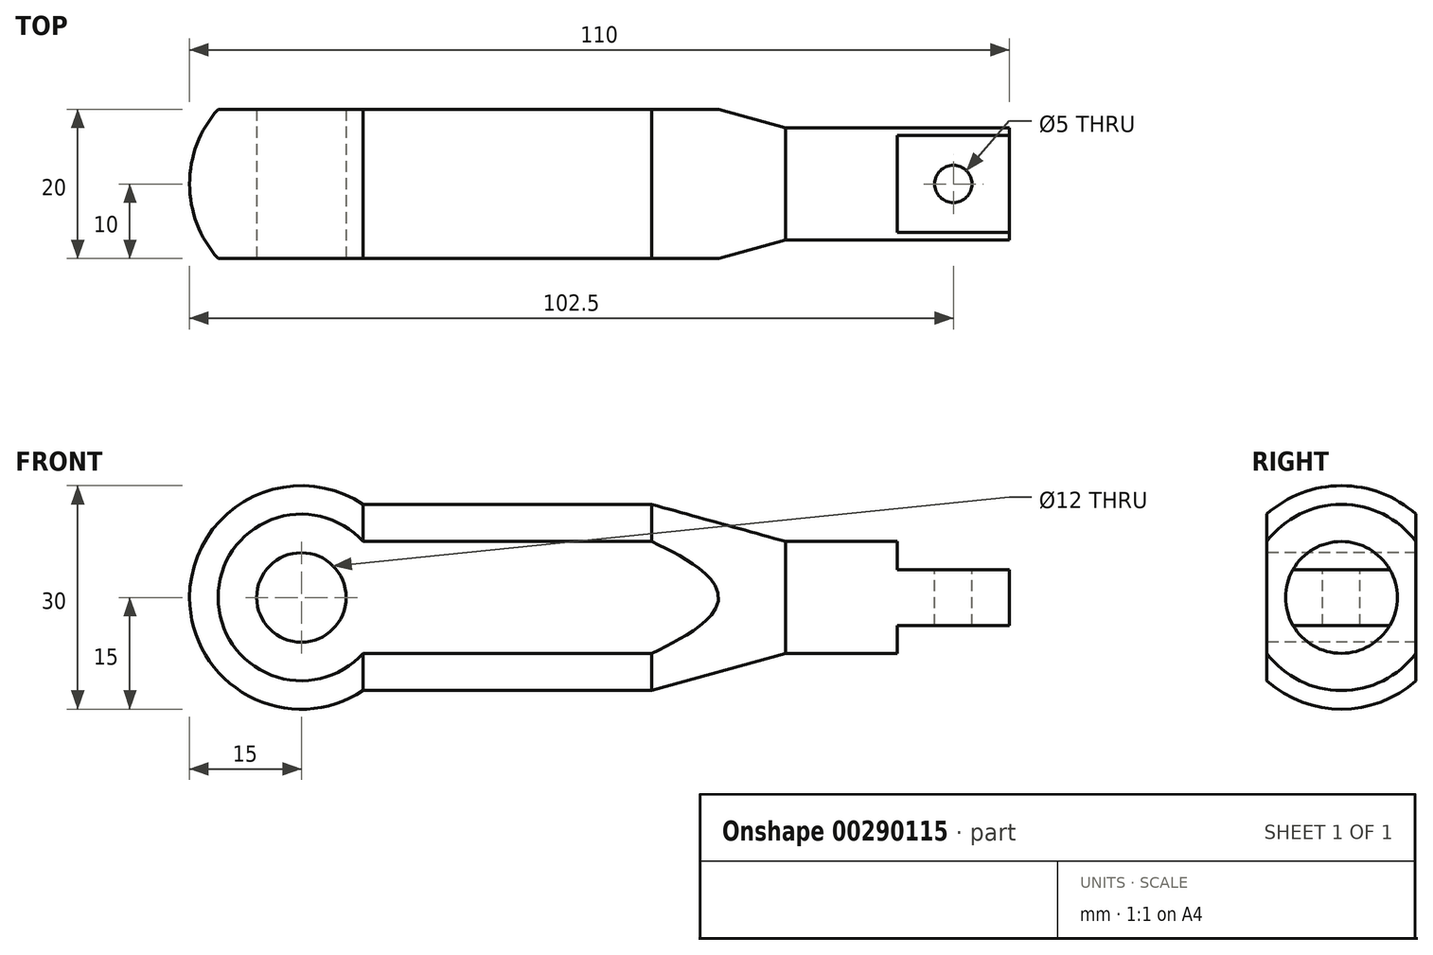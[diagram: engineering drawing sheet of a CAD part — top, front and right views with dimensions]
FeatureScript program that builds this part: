
annotation { "Feature Type Name" : "Feature", "Feature Type Description" : "" }
export const myFeature = defineFeature(function(context is Context, id is Id, definition is map)
    precondition{}
    {
        {
            var Q0;
            Q0=qCreatedBy(makeId("Front.planeOp"),FACE);
            var sketch = newSketch(context, id + "F0", { "sketchPlane" : qUnion([Q0])});
            skLineSegment(sketch, "E0", {"start": v(-47.5, 0) * mm, "end": v(47.5, 0) * mm, "construction": true});
            skLineSegment(sketch, "E1", {"start": v(47.5, 7.5) * mm, "end": v(32.5, 7.5) * mm});
            skLineSegment(sketch, "E2", {"start": v(32.5, 7.5) * mm, "end": v(32.5, 7.5) * mm});
            skLineSegment(sketch, "E3", {"start": v(32.5, 7.5) * mm, "end": v(17.5, 7.5) * mm});
            skLineSegment(sketch, "E4", {"start": v(17.5, 7.5) * mm, "end": v(-0.5, 12.5) * mm});
            skLineSegment(sketch, "E5", {"start": v(-0.5, 12.5) * mm, "end": v(-39.2, 12.5) * mm});
            skCircle(sketch, "E6", {"center": v(-47.5, 0) * mm, "radius": 6 * mm});
            skArc(sketch, "E7", {"start": v(-39.2, 12.5) * mm, "mid": v(-54.6, 13.22) * mm, "end": v(-62.5, 0) * mm});
            skLineSegment(sketch, "E8", {"start": v(-62.5, 0) * mm, "end": v(47.5, 0) * mm});
            skLineSegment(sketch, "E9", {"start": v(32.5, 7.5) * mm, "end": v(32.5, 0) * mm});
            skLineSegment(sketch, "E10", {"start": v(32.5, 0) * mm, "end": v(32.5, -7.5) * mm});
            skLineSegment(sketch, "E11", {"start": v(32.5, -7.5) * mm, "end": v(47.5, -7.5) * mm});
            skLineSegment(sketch, "E12", {"start": v(47.5, 7.5) * mm, "end": v(47.5, -7.5) * mm});
            skLineSegment(sketch, "E13", {"start": v(32.5, 3.75) * mm, "end": v(47.5, 3.75) * mm});
            skLineSegment(sketch, "E14", {"start": v(32.5, -3.75) * mm, "end": v(47.5, -3.75) * mm});
            skSolve(sketch);
        }
        {
            var Q0;
            Q0=qCreatedBy(makeId("Right.planeOp"),FACE);
            var sketch = newSketch(context, id + "F1", { "sketchPlane" : qUnion([Q0])});
            skLineSegment(sketch, "E15", {"start": v(-10, 0) * mm, "end": v(10, 0) * mm});
            skLineSegment(sketch, "E16", {"start": v(-10, 20) * mm, "end": v(-10, -20) * mm});
            skLineSegment(sketch, "E17", {"start": v(10, 20) * mm, "end": v(10, -20) * mm});
            skLineSegment(sketch, "E18", {"start": v(10, 20) * mm, "end": v(60, 20) * mm});
            skLineSegment(sketch, "E19", {"start": v(60, 20) * mm, "end": v(60, -20) * mm});
            skLineSegment(sketch, "E20", {"start": v(60, -20) * mm, "end": v(10, -20) * mm});
            skLineSegment(sketch, "E21", {"start": v(-10, 20) * mm, "end": v(-60, 20) * mm});
            skLineSegment(sketch, "E22", {"start": v(-60, 20) * mm, "end": v(-60, -20) * mm});
            skLineSegment(sketch, "E23", {"start": v(-60, -20) * mm, "end": v(-10, -20) * mm});
            skSolve(sketch);
        }
        {
            var Q0;
            Q0=makeQuery(id+"F0.imprint","IMPRINT",FACE,{"disambiguationData":[TD([[makeQuery(id+"F0.imprint","IMPRINT",EDGE,{"derivedFrom":sQuery(id+"F0.wireOp",EDGE,"E3")}),1.0]])]});
            var Q1;
            {var subQ0=sQuery(id+"F0.wireOp",EDGE,"E1");Q1=makeQuery(id+"F0.imprint","IMPRINT",FACE,{"disambiguationData":[TD([[makeQuery(id+"F0.imprint","IMPRINT",EDGE,{"derivedFrom":subQ0}),1.0]])]});}
            var Q2;
            {var subQ5=sQuery(id+"F0.wireOp",EDGE,"E13");Q2=makeQuery(id+"F0.imprint","IMPRINT",FACE,{"disambiguationData":[TD([[makeQuery(id+"F0.imprint","IMPRINT",EDGE,{"derivedFrom":subQ5}),-1.0]])]});}
            var Q3;
            Q3=sQuery(id+"F0.wireOp",EDGE,"E8");
            revolve(context, id + "F2", {"entities" : qUnion([Q0, Q1, Q2]), "axis" : qUnion([Q3]), "revolveType" : RevolveType.FULL});
        }
        {
            var Q0;
            {var subQ0=sQuery(id+"F0.wireOp",EDGE,"E8");var subQ1=sQuery(id+"F0.wireOp",EDGE,"E6");var subQ2=makeQuery(id+"F0.imprint","INTERSECT",VERTEX,{"disambiguationData":[OD(0.0)],"derivedFrom":[subQ1,subQ0]});Q0=makeQuery(id+"F0.imprint","IMPRINT",FACE,{"disambiguationData":[TD([[makeQuery(id+"F0.imprint","IMPRINT",EDGE,{"disambiguationData":[TD([[subQ2,1.0]])],"derivedFrom":subQ1}),1.0]])]});}
            var Q1;
            {var subQ0=sQuery(id+"F0.wireOp",EDGE,"E8");var subQ1=sQuery(id+"F0.wireOp",EDGE,"E6");var subQ2=makeQuery(id+"F0.imprint","INTERSECT",VERTEX,{"disambiguationData":[OD(0.0)],"derivedFrom":[subQ1,subQ0]});Q1=makeQuery(id+"F0.imprint","IMPRINT",FACE,{"disambiguationData":[TD([[makeQuery(id+"F0.imprint","IMPRINT",EDGE,{"disambiguationData":[TD([[subQ2,-1.0]])],"derivedFrom":subQ1}),1.0]])]});}
            extrude(context, id + "F3", {"entities" : qUnion([Q0, Q1]), "operationType" : NewBodyOperationType.REMOVE, "endBound" : BoundingType.THROUGH_ALL, "oppositeDirection" : true, "depth" : 25 * mm, "hasSecondDirection" : true, "secondDirectionBound" : SecondDirectionBoundingType.THROUGH_ALL, "secondDirectionOppositeDirection" : false, "secondDirectionDepth" : 25 * mm});
        }
        {
            var Q0;
            {var subQ0=sQuery(id+"F0.wireOp",EDGE,"E1");Q0=makeQuery(id+"F0.imprint","IMPRINT",FACE,{"disambiguationData":[TD([[makeQuery(id+"F0.imprint","IMPRINT",EDGE,{"derivedFrom":subQ0}),1.0]])]});}
            var Q1;
            {var subQ0=sQuery(id+"F0.wireOp",EDGE,"E11");Q1=makeQuery(id+"F0.imprint","IMPRINT",FACE,{"disambiguationData":[TD([[makeQuery(id+"F0.imprint","IMPRINT",EDGE,{"derivedFrom":subQ0}),1.0]])]});}
            extrude(context, id + "F4", {"entities" : qUnion([Q0, Q1]), "operationType" : NewBodyOperationType.REMOVE, "depth" : 10.5 * mm, "hasSecondDirection" : true, "secondDirectionBound" : SecondDirectionBoundingType.THROUGH_ALL, "secondDirectionOppositeDirection" : true, "secondDirectionDepth" : 25 * mm});
        }
        {
            var Q0;
            {var subQ0=sQuery(id+"F1.wireOp",EDGE,"E18");Q0=makeQuery(id+"F1.imprint","IMPRINT",FACE,{"disambiguationData":[TD([[makeQuery(id+"F1.imprint","IMPRINT",EDGE,{"derivedFrom":subQ0}),-1.0]])]});}
            var Q1;
            {var subQ0=sQuery(id+"F1.wireOp",EDGE,"E21");Q1=makeQuery(id+"F1.imprint","IMPRINT",FACE,{"disambiguationData":[TD([[makeQuery(id+"F1.imprint","IMPRINT",EDGE,{"derivedFrom":subQ0}),1.0]])]});}
            extrude(context, id + "F5", {"entities" : qUnion([Q0, Q1]), "operationType" : NewBodyOperationType.REMOVE, "endBound" : BoundingType.THROUGH_ALL, "depth" : 25 * mm, "hasSecondDirection" : true, "secondDirectionBound" : SecondDirectionBoundingType.THROUGH_ALL, "secondDirectionOppositeDirection" : true, "secondDirectionDepth" : 25 * mm});
        }
        {
            var Q0;
            Q0=makeQuery(id+"F4.boolean.opBoolean","COPY",FACE,{"derivedFrom":makeQuery(id+"F4.opExtrude","SWEPT_FACE",FACE,{"disambiguationData":[OSD([sQuery(id+"F0.wireOp",EDGE,"E13")])]})});
            var sketch = newSketch(context, id + "F6", { "sketchPlane" : qUnion([Q0])});
            skCircle(sketch, "E24", {"center": v(40, 0) * mm, "radius": 2.5 * mm});
            skSolve(sketch);
        }
        {
            var Q0;
            Q0=makeQuery(id+"F6.imprint","IMPRINT",FACE,{"disambiguationData":[TD([[makeQuery(id+"F6.imprint","IMPRINT",EDGE,{"derivedFrom":sQuery(id+"F6.wireOp",EDGE,"E24")}),1.0]])]});
            extrude(context, id + "F7", {"entities" : qUnion([Q0]), "operationType" : NewBodyOperationType.REMOVE, "endBound" : BoundingType.THROUGH_ALL, "oppositeDirection" : true, "depth" : 25 * mm});
        }
    });
